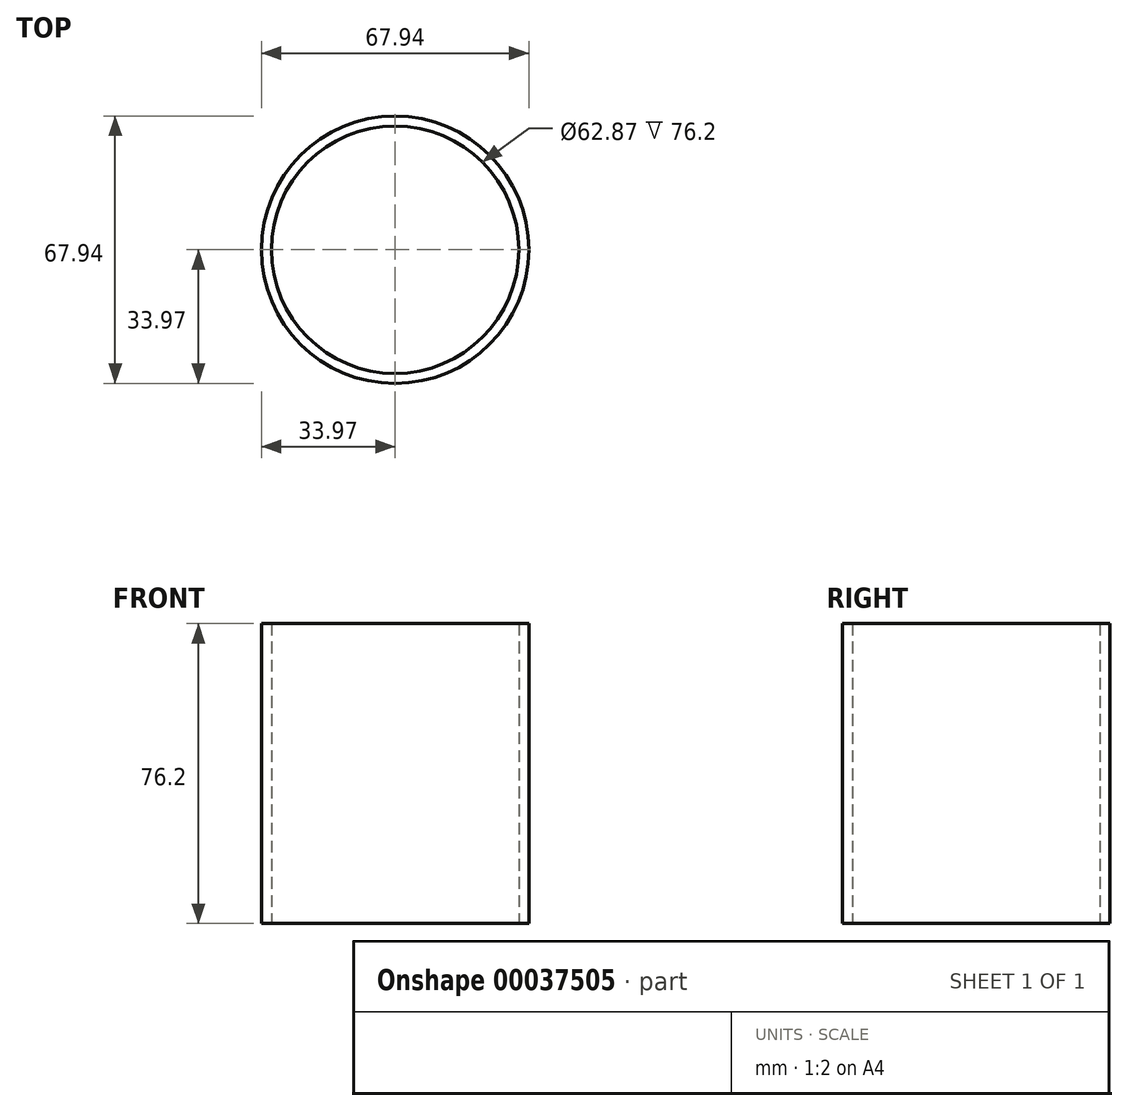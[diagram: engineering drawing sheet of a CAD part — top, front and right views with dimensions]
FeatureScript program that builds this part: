
annotation { "Feature Type Name" : "Feature", "Feature Type Description" : "" }
export const myFeature = defineFeature(function(context is Context, id is Id, definition is map)
    precondition{}
    {
        {
            var Q0;
            Q0=qCreatedBy(makeId("Top.planeOp"),FACE);
            var sketch = newSketch(context, id + "F0", { "sketchPlane" : qUnion([Q0])});
            skCircle(sketch, "E0", {"center": v(0, 0) * mm, "radius": 31.43 * mm});
            skCircle(sketch, "E1", {"center": v(0, 0) * mm, "radius": 33.97 * mm});
            skSolve(sketch);
        }
        {
            var Q0;
            Q0=makeQuery(id+"F0.imprint","IMPRINT",FACE,{"disambiguationData":[TD([[makeQuery(id+"F0.imprint","IMPRINT",EDGE,{"derivedFrom":sQuery(id+"F0.wireOp",EDGE,"E0")}),-1.0]])]});
            extrude(context, id + "F1", {"entities" : qUnion([Q0]), "depth" : 76.2 * mm});
        }
    });
